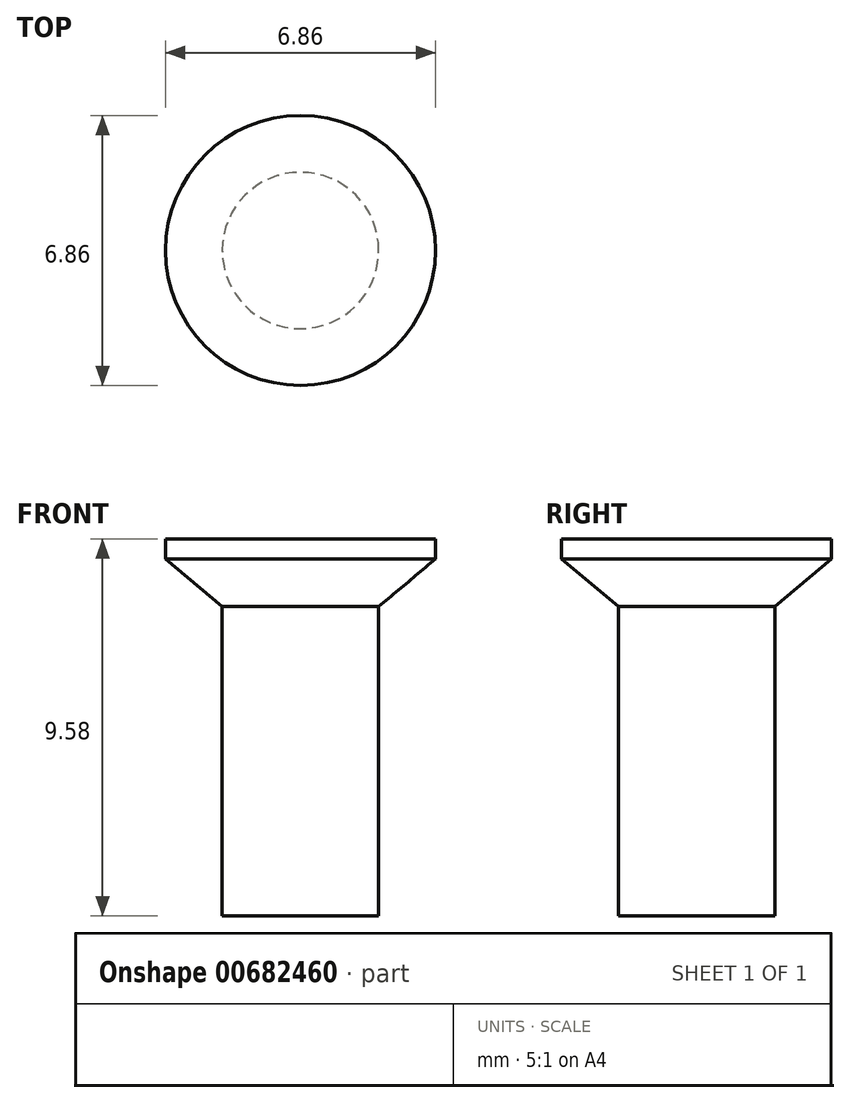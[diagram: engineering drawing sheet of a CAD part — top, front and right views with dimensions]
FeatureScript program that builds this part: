
annotation { "Feature Type Name" : "Feature", "Feature Type Description" : "" }
export const myFeature = defineFeature(function(context is Context, id is Id, definition is map)
    precondition{}
    {
        {
            var Q0;
            Q0=qCreatedBy(makeId("Front.planeOp"),FACE);
            var sketch = newSketch(context, id + "F0", { "sketchPlane" : qUnion([Q0])});
            skLineSegment(sketch, "E0", {"start": v(0, 0) * mm, "end": v(-3.43, 0) * mm});
            skLineSegment(sketch, "E1", {"start": v(-3.43, 0) * mm, "end": v(-3.43, -0.5) * mm});
            skLineSegment(sketch, "E2", {"start": v(-3.43, -0.5) * mm, "end": v(-1.99, -1.72) * mm});
            skLineSegment(sketch, "E3", {"start": v(-1.99, -1.72) * mm, "end": v(-1.99, -9.58) * mm});
            skLineSegment(sketch, "E4", {"start": v(-1.99, -9.58) * mm, "end": v(0, -9.58) * mm});
            skLineSegment(sketch, "E5", {"start": v(0, -9.58) * mm, "end": v(0, 0) * mm});
            skLineSegment(sketch, "E6", {"start": v(-3.43, -0.5) * mm, "end": v(2.23, -0.5) * mm, "construction": true});
            skLineSegment(sketch, "E7", {"start": v(-1.99, -1.72) * mm, "end": v(-1.99, -0.5) * mm, "construction": true});
            skLineSegment(sketch, "E8", {"start": v(0, 74.6) * mm, "end": v(0, -51.12) * mm, "construction": true});
            skSolve(sketch);
        }
        {
            var Q0;
            Q0 = qSketchRegion(id + "F0", true);
            var Q1;
            Q1=sQuery(id+"F0.wireOp",EDGE,"E8");
            revolve(context, id + "F1", {"entities" : qUnion([Q0]), "axis" : qUnion([Q1]), "revolveType" : RevolveType.FULL});
        }
    });
